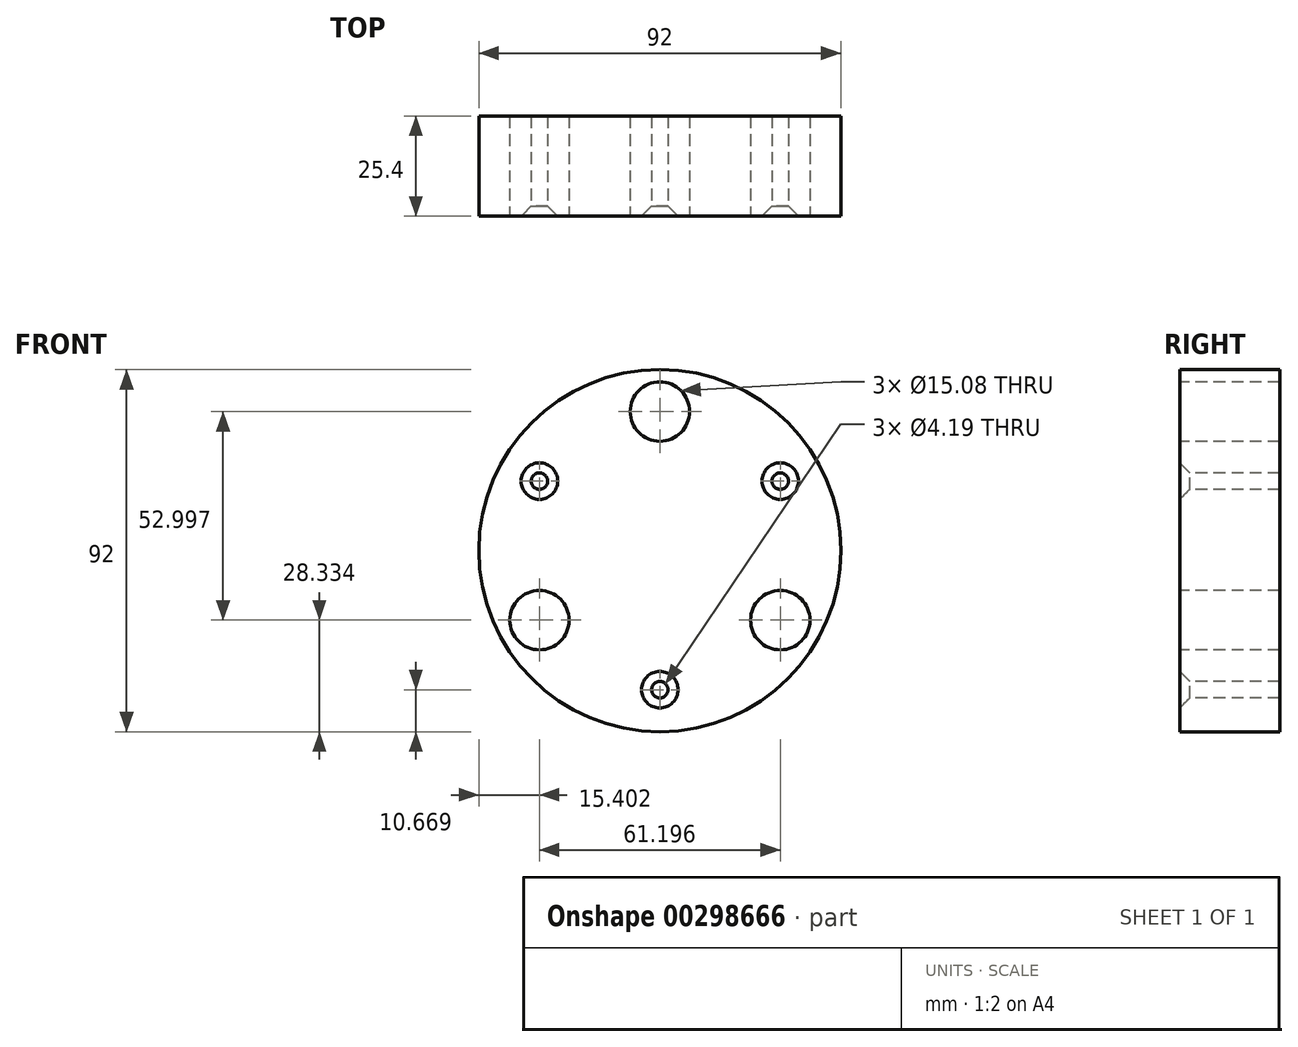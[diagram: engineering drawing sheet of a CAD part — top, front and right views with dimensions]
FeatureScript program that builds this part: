
annotation { "Feature Type Name" : "Feature", "Feature Type Description" : "" }
export const myFeature = defineFeature(function(context is Context, id is Id, definition is map)
    precondition{}
    {
        {
            var Q0;
            Q0=qCreatedBy(makeId("Front.planeOp"),FACE);
            var sketch = newSketch(context, id + "F0", { "sketchPlane" : qUnion([Q0])});
            skCircle(sketch, "E0", {"center": v(0, 0) * mm, "radius": 46 * mm});
            skCircle(sketch, "E1", {"center": v(0, 0) * mm, "radius": 35.33 * mm, "construction": true});
            skLineSegment(sketch, "E2.0", {"start": v(0, 35.33) * mm, "end": v(30.6, -17.67) * mm, "construction": true});
            skLineSegment(sketch, "E2.1", {"start": v(30.6, -17.67) * mm, "end": v(-30.6, -17.67) * mm, "construction": true});
            skLineSegment(sketch, "E2.2", {"start": v(-30.6, -17.67) * mm, "end": v(0, 35.33) * mm, "construction": true});
            skCircle(sketch, "E3", {"center": v(0, 35.33) * mm, "radius": 7.54 * mm});
            skCircle(sketch, "E4", {"center": v(30.6, -17.67) * mm, "radius": 7.54 * mm});
            skCircle(sketch, "E5", {"center": v(-30.6, -17.67) * mm, "radius": 7.54 * mm});
            skLineSegment(sketch, "E6.0", {"start": v(0, 35.33) * mm, "end": v(30.6, 17.67) * mm, "construction": true});
            skLineSegment(sketch, "E6.1", {"start": v(30.6, 17.67) * mm, "end": v(30.6, -17.67) * mm, "construction": true});
            skLineSegment(sketch, "E6.2", {"start": v(30.6, -17.67) * mm, "end": v(0, -35.33) * mm, "construction": true});
            skLineSegment(sketch, "E6.3", {"start": v(0, -35.33) * mm, "end": v(-30.6, -17.67) * mm, "construction": true});
            skLineSegment(sketch, "E6.4", {"start": v(-30.6, -17.67) * mm, "end": v(-30.6, 17.67) * mm, "construction": true});
            skLineSegment(sketch, "E6.5", {"start": v(-30.6, 17.67) * mm, "end": v(0, 35.33) * mm, "construction": true});
            skCircle(sketch, "E7", {"center": v(-30.6, 17.67) * mm, "radius": 2.1 * mm});
            skCircle(sketch, "E8", {"center": v(30.6, 17.67) * mm, "radius": 2.1 * mm});
            skCircle(sketch, "E9", {"center": v(0, -35.33) * mm, "radius": 2.1 * mm});
            skSolve(sketch);
        }
        {
            var Q0;
            Q0=makeQuery(id+"F0.imprint","IMPRINT",FACE,{"disambiguationData":[TD([[makeQuery(id+"F0.imprint","IMPRINT",EDGE,{"derivedFrom":sQuery(id+"F0.wireOp",EDGE,"E0")}),1.0]])]});
            extrude(context, id + "F1", {"entities" : qUnion([Q0]), "oppositeDirection" : true, "depth" : 25.4 * mm});
        }
        {
            var Q0;
            Q0=makeQuery(id+"F1.opExtrude","CAP_EDGE",EDGE,{"disambiguationData":[OSD([sQuery(id+"F0.wireOp",EDGE,"E7")])],"isStart":true});
            chamfer(context, id + "F2", {"entities" : qUnion([Q0]), "width" : 2.54 * mm, "tangentPropagation" : true});
        }
        {
            var Q0;
            Q0=makeQuery(id+"F1.opExtrude","CAP_EDGE",EDGE,{"disambiguationData":[OSD([sQuery(id+"F0.wireOp",EDGE,"E8")])],"isStart":true});
            chamfer(context, id + "F3", {"entities" : qUnion([Q0]), "width" : 2.54 * mm, "tangentPropagation" : true});
        }
        {
            var Q0;
            Q0=makeQuery(id+"F1.opExtrude","CAP_EDGE",EDGE,{"disambiguationData":[OSD([sQuery(id+"F0.wireOp",EDGE,"E9")])],"isStart":true});
            chamfer(context, id + "F4", {"entities" : qUnion([Q0]), "width" : 2.54 * mm, "tangentPropagation" : true});
        }
    });
